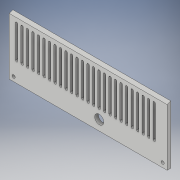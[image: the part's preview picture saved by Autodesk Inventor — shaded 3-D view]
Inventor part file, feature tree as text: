
AUTODESK INVENTOR PART (.ipt)
format: ipt  version: 2019 (Build 230136000, 136)  size: 203,264 bytes
history: native  units: mm
features: sketch x5, extrude x3, hole x2, pattern_linear x1
ambient origin geometry x8: Origin, YZ Plane, XZ Plane, XY Plane, X Axis, Y Axis, Z Axis, Center Point
bodies: Volumenkörper1 (feature_tree)
feature tree (11):
  extrude  "Extrusion1"  Depth=172.2mm
  extrude  "Extrusion2"  Depth=4.0mm
  hole  "Bohrung1"  [1 undecoded]
  hole  "Bohrung2"  [1 undecoded]
  extrude  "Extrusion3"  Depth=6.0mm
  pattern_linear  "Rechteckige Anordnung1"  Spacing1=35.0mm  [1 undecoded]
  sketch  "Skizze1"  dims[d0=62.0mm d1=172.2mm]
  sketch  "Skizze2"  dims[d2=4.0mm d3=0.0mm d4=3.490659mm]
  sketch  "Skizze3"  dims[d5=4.0mm d6=0.0mm d7=74.0mm]
  sketch  "Skizze4"  dims[d8=11.0mm]
  sketch  "Skizze5"  dims[d9=10.0mm d10=6.0mm d11=3.023mm d12=2.0mm d13=14.3117mm d14=15.0mm d15=20.594885mm d16=162.406mm d17=4.9mm d18=3.4mm d19=6.0mm d20=6.3mm d21=2.0mm d22=90.0deg d23=15.0mm d24=20.594885mm d25=35.0mm d26=8.0mm d27=4.0mm d28=0.0mm d29=260.0mm d31=6.0mm]
note: 3 required parameter values undecoded (feature->parameter linkage not recoverable at this tier; creation-order binding heuristic only, values carry confidence <= 0.55)
